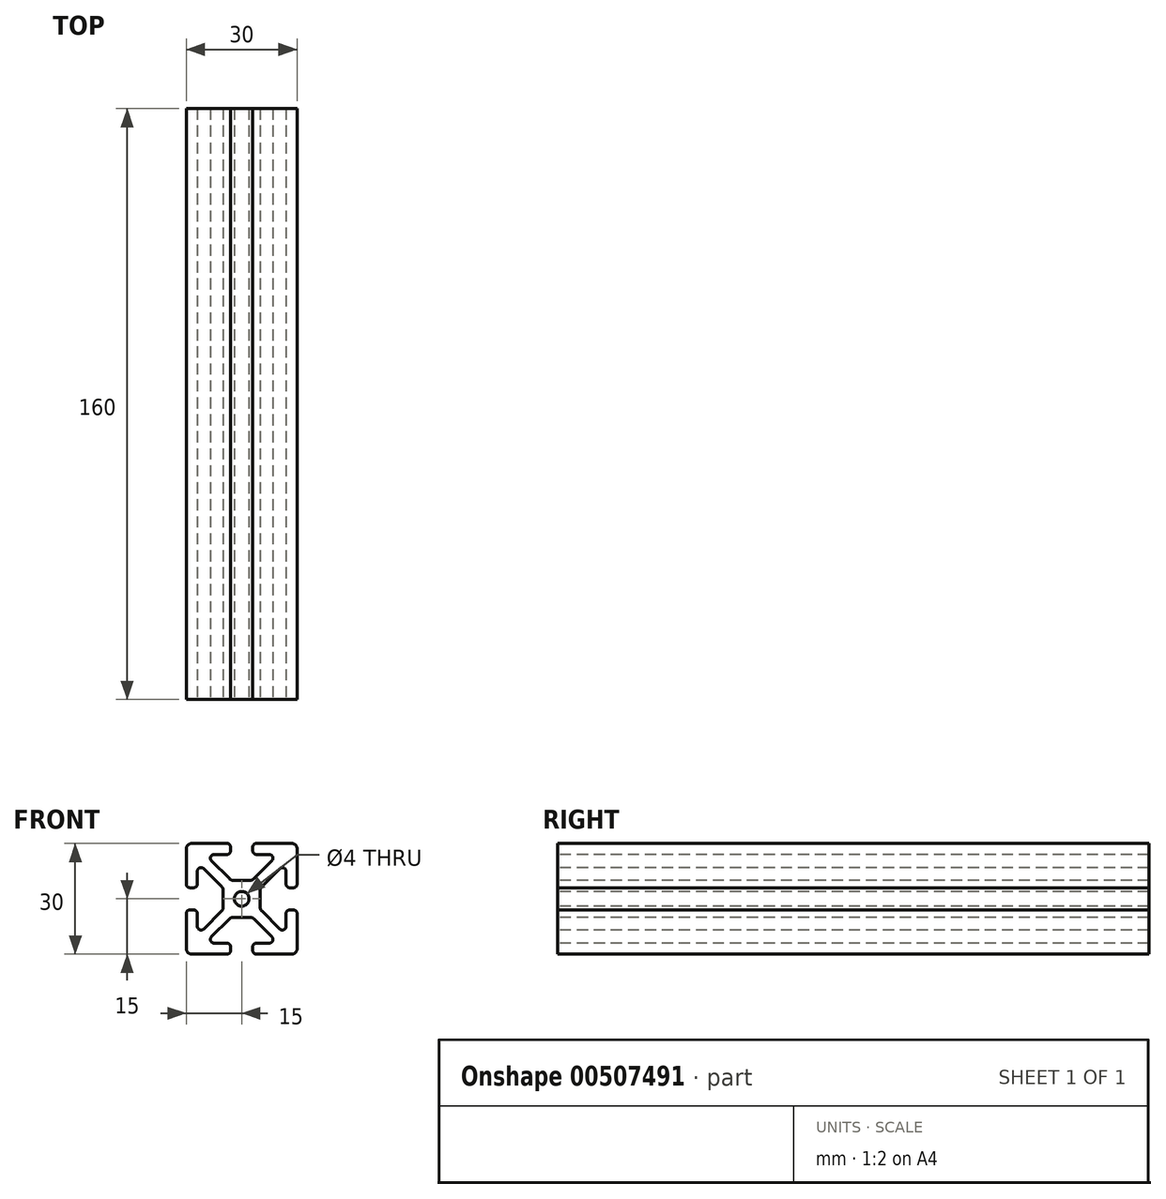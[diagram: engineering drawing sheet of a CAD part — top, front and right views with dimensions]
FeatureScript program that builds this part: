
annotation { "Feature Type Name" : "Feature", "Feature Type Description" : "" }
export const myFeature = defineFeature(function(context is Context, id is Id, definition is map)
    precondition{}
    {
        {
            var Q0;
            Q0=qCreatedBy(makeId("Front.planeOp"),FACE);
            var sketch = newSketch(context, id + "F0", { "sketchPlane" : qUnion([Q0])});
            skLineSegment(sketch, "E0.bottom", {"start": v(13.5, 15) * mm, "end": v(4, 15) * mm});
            skLineSegment(sketch, "E0.top", {"start": v(13.5, -15) * mm, "end": v(4, -15) * mm});
            skLineSegment(sketch, "E0.left", {"start": v(15, 13.5) * mm, "end": v(15, 4) * mm});
            skLineSegment(sketch, "E0.right", {"start": v(-15, 13.5) * mm, "end": v(-15, 4) * mm});
            skPoint(sketch, "E0.middle", {"position": v(0, 0) * mm});
            skLineSegment(sketch, "E1.bottom", {"start": v(7.46, 12) * mm, "end": v(4, 12) * mm});
            skLineSegment(sketch, "E1.top", {"start": v(7.46, -12) * mm, "end": v(4, -12) * mm});
            skLineSegment(sketch, "E1.left", {"start": v(12, 7.46) * mm, "end": v(12, 4) * mm});
            skLineSegment(sketch, "E1.right", {"start": v(-12, 7.46) * mm, "end": v(-12, 4) * mm});
            skLineSegment(sketch, "E2", {"start": v(8.17, 10.3) * mm, "end": v(3.32, 5.44) * mm});
            skLineSegment(sketch, "E3", {"start": v(-8.17, -10.3) * mm, "end": v(-3.32, -5.44) * mm});
            skLineSegment(sketch, "E4", {"start": v(-8.17, 10.3) * mm, "end": v(-3.32, 5.44) * mm});
            skLineSegment(sketch, "E5", {"start": v(-10.3, 8.17) * mm, "end": v(-5.44, 3.32) * mm});
            skPoint(sketch, "E6.orphan", {"position": v(12, 12) * mm});
            skPoint(sketch, "E7.orphan", {"position": v(12, -12) * mm});
            skPoint(sketch, "E8.orphan", {"position": v(-12, -12) * mm});
            skPoint(sketch, "E9.orphan", {"position": v(-12, 12) * mm});
            skLineSegment(sketch, "E10.trimOffspring", {"start": v(-5.44, -3.32) * mm, "end": v(-10.3, -8.17) * mm});
            skLineSegment(sketch, "E11.trimOffspring", {"start": v(5.44, -3.32) * mm, "end": v(10.3, -8.17) * mm});
            skLineSegment(sketch, "E12.trimOffspring", {"start": v(5.44, 3.32) * mm, "end": v(10.3, 8.17) * mm});
            skLineSegment(sketch, "E13.trimOffspring", {"start": v(3.32, -5.44) * mm, "end": v(8.17, -10.3) * mm});
            skLineSegment(sketch, "E14.bottom", {"start": v(2.26, 5) * mm, "end": v(-2.26, 5) * mm});
            skLineSegment(sketch, "E14.top", {"start": v(2.26, -5) * mm, "end": v(-2.26, -5) * mm});
            skLineSegment(sketch, "E14.left", {"start": v(5, 2.26) * mm, "end": v(5, -2.26) * mm});
            skLineSegment(sketch, "E14.right", {"start": v(-5, 2.26) * mm, "end": v(-5, -2.26) * mm});
            skPoint(sketch, "E15.orphan", {"position": v(5, 5) * mm});
            skPoint(sketch, "E16.orphan", {"position": v(5, -5) * mm});
            skPoint(sketch, "E17.orphan", {"position": v(-5, -5) * mm});
            skPoint(sketch, "E18.orphan", {"position": v(-5, 5) * mm});
            skCircle(sketch, "E19", {"center": v(0, 0) * mm, "radius": 2 * mm});
            skLineSegment(sketch, "E20", {"start": v(-3, 14) * mm, "end": v(-3, 13) * mm});
            skLineSegment(sketch, "E21", {"start": v(3, 14) * mm, "end": v(3, 13) * mm});
            skLineSegment(sketch, "E22.trimOffspring", {"start": v(-3, -13) * mm, "end": v(-3, -14) * mm});
            skLineSegment(sketch, "E23.trimOffspring", {"start": v(-4, 12) * mm, "end": v(-7.46, 12) * mm});
            skLineSegment(sketch, "E24.trimOffspring", {"start": v(-4, 15) * mm, "end": v(-13.5, 15) * mm});
            skLineSegment(sketch, "E25.trimOffspring", {"start": v(3, -13) * mm, "end": v(3, -14) * mm});
            skLineSegment(sketch, "E26.trimOffspring", {"start": v(-4, -12) * mm, "end": v(-7.46, -12) * mm});
            skLineSegment(sketch, "E27.trimOffspring", {"start": v(-4, -15) * mm, "end": v(-13.5, -15) * mm});
            skLineSegment(sketch, "E28", {"start": v(-14, 3) * mm, "end": v(-13, 3) * mm});
            skLineSegment(sketch, "E29", {"start": v(-14, -3) * mm, "end": v(-13, -3) * mm});
            skLineSegment(sketch, "E30.trimOffspring", {"start": v(-12, -4) * mm, "end": v(-12, -7.46) * mm});
            skLineSegment(sketch, "E31.trimOffspring", {"start": v(-15, -4) * mm, "end": v(-15, -13.5) * mm});
            skLineSegment(sketch, "E32.trimOffspring", {"start": v(13, 3) * mm, "end": v(14, 3) * mm});
            skLineSegment(sketch, "E33.trimOffspring", {"start": v(13, -3) * mm, "end": v(14, -3) * mm});
            skLineSegment(sketch, "E34.trimOffspring", {"start": v(12, -4) * mm, "end": v(12, -7.46) * mm});
            skLineSegment(sketch, "E35.trimOffspring", {"start": v(15, -4) * mm, "end": v(15, -13.5) * mm});
            skPoint(sketch, "E36.visualSharp", {"position": v(-15, 15) * mm});
            skArc(sketch, "E36.filletArc", {"start": v(-13.5, 15) * mm, "mid": v(-14.56, 14.56) * mm, "end": v(-15, 13.5) * mm});
            skPoint(sketch, "E37.visualSharp", {"position": v(15, 15) * mm});
            skArc(sketch, "E37.filletArc", {"start": v(15, 13.5) * mm, "mid": v(14.56, 14.56) * mm, "end": v(13.5, 15) * mm});
            skPoint(sketch, "E38.visualSharp", {"position": v(15, -15) * mm});
            skArc(sketch, "E38.filletArc", {"start": v(13.5, -15) * mm, "mid": v(14.56, -14.56) * mm, "end": v(15, -13.5) * mm});
            skPoint(sketch, "E39.visualSharp", {"position": v(-15, -15) * mm});
            skArc(sketch, "E39.filletArc", {"start": v(-15, -13.5) * mm, "mid": v(-14.56, -14.56) * mm, "end": v(-13.5, -15) * mm});
            skPoint(sketch, "E40.visualSharp", {"position": v(-5, -2.88) * mm});
            skArc(sketch, "E40.filletArc", {"start": v(-5.44, -3.32) * mm, "mid": v(-5.11, -2.83) * mm, "end": v(-5, -2.26) * mm});
            skPoint(sketch, "E41.visualSharp", {"position": v(-2.88, -5) * mm});
            skArc(sketch, "E41.filletArc", {"start": v(-2.26, -5) * mm, "mid": v(-2.83, -5.11) * mm, "end": v(-3.32, -5.44) * mm});
            skPoint(sketch, "E42.visualSharp", {"position": v(2.88, -5) * mm});
            skArc(sketch, "E42.filletArc", {"start": v(3.32, -5.44) * mm, "mid": v(2.83, -5.11) * mm, "end": v(2.26, -5) * mm});
            skPoint(sketch, "E43.visualSharp", {"position": v(5, -2.88) * mm});
            skArc(sketch, "E43.filletArc", {"start": v(5, -2.26) * mm, "mid": v(5.11, -2.83) * mm, "end": v(5.44, -3.32) * mm});
            skPoint(sketch, "E44.visualSharp", {"position": v(5, 2.88) * mm});
            skArc(sketch, "E44.filletArc", {"start": v(5.44, 3.32) * mm, "mid": v(5.11, 2.83) * mm, "end": v(5, 2.26) * mm});
            skPoint(sketch, "E45.visualSharp", {"position": v(2.88, 5) * mm});
            skArc(sketch, "E45.filletArc", {"start": v(2.26, 5) * mm, "mid": v(2.83, 5.11) * mm, "end": v(3.32, 5.44) * mm});
            skPoint(sketch, "E46.visualSharp", {"position": v(-2.88, 5) * mm});
            skArc(sketch, "E46.filletArc", {"start": v(-3.32, 5.44) * mm, "mid": v(-2.83, 5.11) * mm, "end": v(-2.26, 5) * mm});
            skPoint(sketch, "E47.visualSharp", {"position": v(-3, 12) * mm});
            skArc(sketch, "E47.filletArc", {"start": v(-4, 12) * mm, "mid": v(-3.3, 12.3) * mm, "end": v(-3, 13) * mm});
            skPoint(sketch, "E48.visualSharp", {"position": v(-3, 15) * mm});
            skArc(sketch, "E48.filletArc", {"start": v(-3, 14) * mm, "mid": v(-3.3, 14.7) * mm, "end": v(-4, 15) * mm});
            skPoint(sketch, "E49.visualSharp", {"position": v(3, 15) * mm});
            skArc(sketch, "E49.filletArc", {"start": v(4, 15) * mm, "mid": v(3.3, 14.7) * mm, "end": v(3, 14) * mm});
            skPoint(sketch, "E50.visualSharp", {"position": v(3, 12) * mm});
            skArc(sketch, "E50.filletArc", {"start": v(3, 13) * mm, "mid": v(3.3, 12.3) * mm, "end": v(4, 12) * mm});
            skPoint(sketch, "E51.visualSharp", {"position": v(12, 3) * mm});
            skArc(sketch, "E51.filletArc", {"start": v(12, 4) * mm, "mid": v(12.3, 3.3) * mm, "end": v(13, 3) * mm});
            skPoint(sketch, "E52.visualSharp", {"position": v(15, 3) * mm});
            skArc(sketch, "E52.filletArc", {"start": v(14, 3) * mm, "mid": v(14.7, 3.3) * mm, "end": v(15, 4) * mm});
            skPoint(sketch, "E53.visualSharp", {"position": v(15, -3) * mm});
            skArc(sketch, "E53.filletArc", {"start": v(15, -4) * mm, "mid": v(14.7, -3.3) * mm, "end": v(14, -3) * mm});
            skPoint(sketch, "E54.visualSharp", {"position": v(12, -3) * mm});
            skArc(sketch, "E54.filletArc", {"start": v(13, -3) * mm, "mid": v(12.3, -3.3) * mm, "end": v(12, -4) * mm});
            skPoint(sketch, "E55.visualSharp", {"position": v(3, -12) * mm});
            skArc(sketch, "E55.filletArc", {"start": v(4, -12) * mm, "mid": v(3.3, -12.3) * mm, "end": v(3, -13) * mm});
            skPoint(sketch, "E56.visualSharp", {"position": v(3, -15) * mm});
            skArc(sketch, "E56.filletArc", {"start": v(3, -14) * mm, "mid": v(3.3, -14.7) * mm, "end": v(4, -15) * mm});
            skPoint(sketch, "E57.visualSharp", {"position": v(-3, -12) * mm});
            skArc(sketch, "E57.filletArc", {"start": v(-3, -13) * mm, "mid": v(-3.3, -12.3) * mm, "end": v(-4, -12) * mm});
            skPoint(sketch, "E58.visualSharp", {"position": v(-3, -15) * mm});
            skArc(sketch, "E58.filletArc", {"start": v(-4, -15) * mm, "mid": v(-3.3, -14.7) * mm, "end": v(-3, -14) * mm});
            skPoint(sketch, "E59.visualSharp", {"position": v(-12, -3) * mm});
            skArc(sketch, "E59.filletArc", {"start": v(-12, -4) * mm, "mid": v(-12.3, -3.3) * mm, "end": v(-13, -3) * mm});
            skPoint(sketch, "E60.visualSharp", {"position": v(-15, -3) * mm});
            skArc(sketch, "E60.filletArc", {"start": v(-14, -3) * mm, "mid": v(-14.7, -3.3) * mm, "end": v(-15, -4) * mm});
            skPoint(sketch, "E61.visualSharp", {"position": v(-15, 3) * mm});
            skArc(sketch, "E61.filletArc", {"start": v(-15, 4) * mm, "mid": v(-14.7, 3.3) * mm, "end": v(-14, 3) * mm});
            skPoint(sketch, "E62.visualSharp", {"position": v(-12, 3) * mm});
            skArc(sketch, "E62.filletArc", {"start": v(-13, 3) * mm, "mid": v(-12.3, 3.3) * mm, "end": v(-12, 4) * mm});
            skPoint(sketch, "E63.visualSharp", {"position": v(9.88, 12) * mm});
            skArc(sketch, "E63.filletArc", {"start": v(8.17, 10.3) * mm, "mid": v(8.39, 11.38) * mm, "end": v(7.46, 12) * mm});
            skPoint(sketch, "E64.visualSharp", {"position": v(12, 9.88) * mm});
            skArc(sketch, "E64.filletArc", {"start": v(12, 7.46) * mm, "mid": v(11.38, 8.39) * mm, "end": v(10.3, 8.17) * mm});
            skPoint(sketch, "E65.visualSharp", {"position": v(12, -9.88) * mm});
            skArc(sketch, "E65.filletArc", {"start": v(10.3, -8.17) * mm, "mid": v(11.38, -8.39) * mm, "end": v(12, -7.46) * mm});
            skPoint(sketch, "E66.visualSharp", {"position": v(9.88, -12) * mm});
            skArc(sketch, "E66.filletArc", {"start": v(7.46, -12) * mm, "mid": v(8.39, -11.38) * mm, "end": v(8.17, -10.3) * mm});
            skPoint(sketch, "E67.visualSharp", {"position": v(-12, -9.88) * mm});
            skArc(sketch, "E67.filletArc", {"start": v(-12, -7.46) * mm, "mid": v(-11.38, -8.39) * mm, "end": v(-10.3, -8.17) * mm});
            skPoint(sketch, "E68.visualSharp", {"position": v(-9.88, -12) * mm});
            skArc(sketch, "E68.filletArc", {"start": v(-8.17, -10.3) * mm, "mid": v(-8.39, -11.38) * mm, "end": v(-7.46, -12) * mm});
            skPoint(sketch, "E69.visualSharp", {"position": v(-12, 9.88) * mm});
            skArc(sketch, "E69.filletArc", {"start": v(-10.3, 8.17) * mm, "mid": v(-11.38, 8.39) * mm, "end": v(-12, 7.46) * mm});
            skPoint(sketch, "E70.visualSharp", {"position": v(-9.88, 12) * mm});
            skArc(sketch, "E70.filletArc", {"start": v(-7.46, 12) * mm, "mid": v(-8.39, 11.38) * mm, "end": v(-8.17, 10.3) * mm});
            skPoint(sketch, "E71.visualSharp", {"position": v(-5, 2.88) * mm});
            skArc(sketch, "E71.filletArc", {"start": v(-5, 2.26) * mm, "mid": v(-5.11, 2.83) * mm, "end": v(-5.44, 3.32) * mm});
            skSolve(sketch);
        }
        {
            var Q0;
            Q0=qSketchRegion(id+"F0",true);
            extrude(context, id + "F1", {"entities" : qUnion([Q0]), "oppositeDirection" : true, "depth" : 160 * mm});
        }
    });
